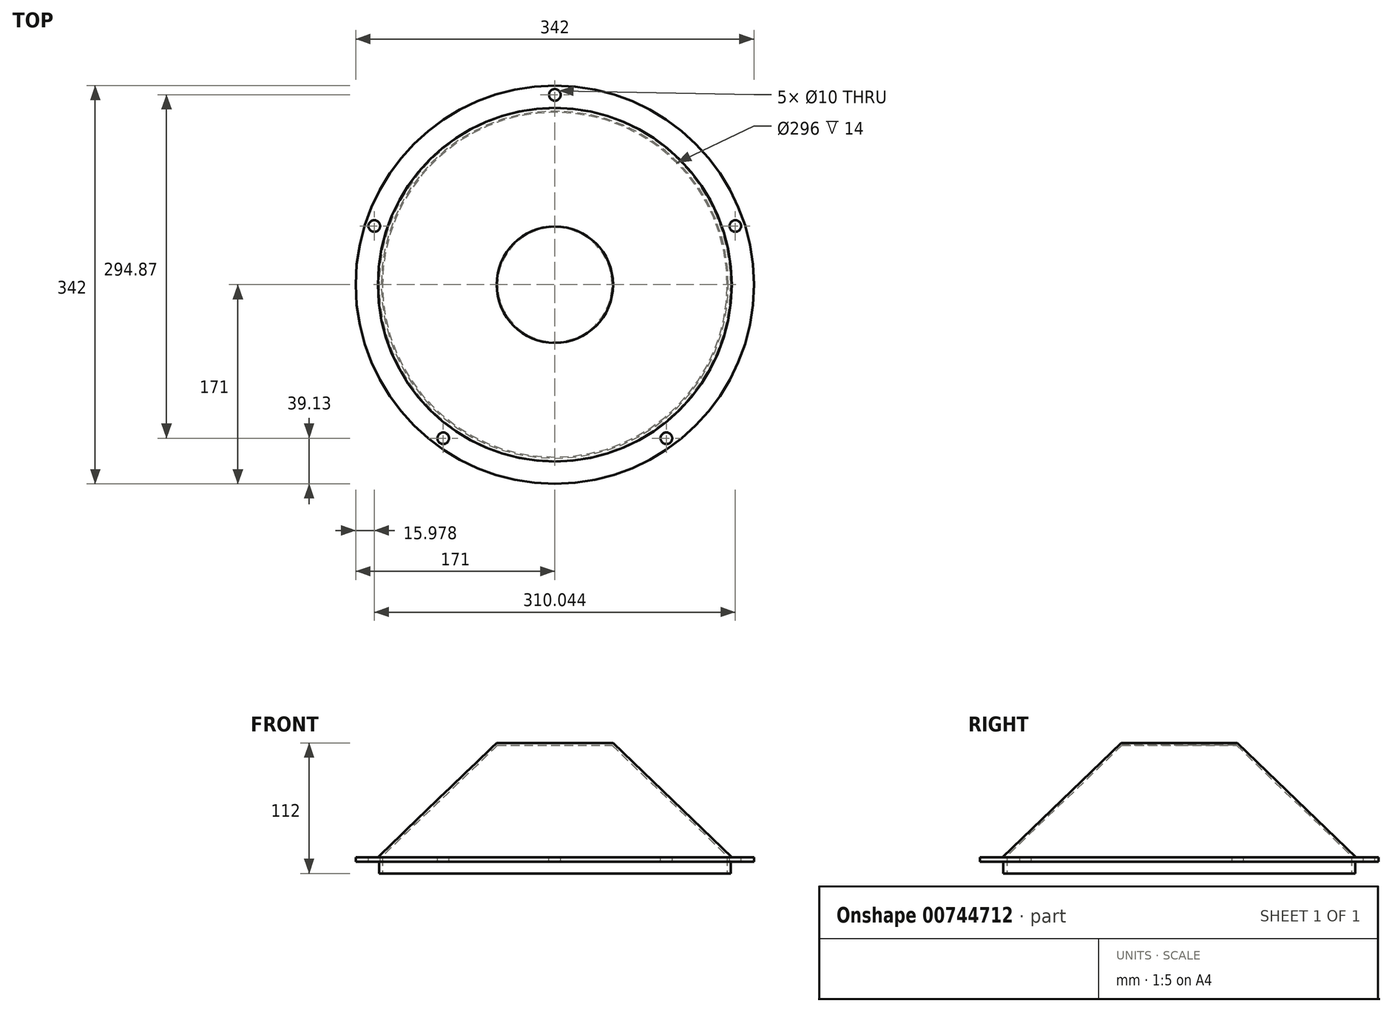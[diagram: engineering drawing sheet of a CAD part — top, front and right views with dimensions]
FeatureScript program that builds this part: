
annotation { "Feature Type Name" : "Feature", "Feature Type Description" : "" }
export const myFeature = defineFeature(function(context is Context, id is Id, definition is map)
    precondition{}
    {
        {
            var Q0;
            Q0=qCreatedBy(makeId("Top.planeOp"),FACE);
            var sketch = newSketch(context, id + "F0", { "sketchPlane" : qUnion([Q0])});
            skCircle(sketch, "E0", {"center": v(0, 0) * mm, "radius": 171 * mm});
            skCircle(sketch, "E1", {"center": v(0, 0) * mm, "radius": 148 * mm});
            skSolve(sketch);
        }
        {
            var Q0;
            Q0 = qSketchRegion(id + "F0", true);
            extrude(context, id + "F1", {"entities" : qUnion([Q0]), "depth" : 4 * mm, "offsetDistance" : 25 * mm});
        }
        {
            var Q0;
            Q0=makeQuery(id+"F1.opExtrude","CAP_FACE",FACE,{"disambiguationData":[OSD([sQuery(id+"F0.wireOp",EDGE,"E0"),sQuery(id+"F0.wireOp",EDGE,"E1")])],"isStart":false});
            var sketch = newSketch(context, id + "F2", { "sketchPlane" : qUnion([Q0])});
            skCircle(sketch, "E2", {"center": v(0, 163) * mm, "radius": 5 * mm});
            skCircle(sketch, "E3.1.0", {"center": v(-155.02, 50.37) * mm, "radius": 5 * mm});
            skCircle(sketch, "E3.2.0", {"center": v(-95.8, -131.87) * mm, "radius": 5 * mm});
            skCircle(sketch, "E3.3.0", {"center": v(95.8, -131.87) * mm, "radius": 5 * mm});
            skCircle(sketch, "E3.4.0", {"center": v(155.02, 50.37) * mm, "radius": 5 * mm});
            skPoint(sketch, "E3.center", {"position": v(0, 0) * mm});
            skSolve(sketch);
        }
        {
            var Q0;
            Q0=makeQuery(id+"F2.imprint","IMPRINT",FACE,{"disambiguationData":[TD([[makeQuery(id+"F2.imprint","IMPRINT",EDGE,{"derivedFrom":sQuery(id+"F2.wireOp",EDGE,"E2")}),1.0]])]});
            var Q1;
            Q1=makeQuery(id+"F2.imprint","IMPRINT",FACE,{"disambiguationData":[TD([[makeQuery(id+"F2.imprint","IMPRINT",EDGE,{"derivedFrom":sQuery(id+"F2.wireOp",EDGE,"E3.1.0")}),1.0]])]});
            var Q2;
            Q2=makeQuery(id+"F2.imprint","IMPRINT",FACE,{"disambiguationData":[TD([[makeQuery(id+"F2.imprint","IMPRINT",EDGE,{"derivedFrom":sQuery(id+"F2.wireOp",EDGE,"E3.4.0")}),1.0]])]});
            var Q3;
            Q3=makeQuery(id+"F2.imprint","IMPRINT",FACE,{"disambiguationData":[TD([[makeQuery(id+"F2.imprint","IMPRINT",EDGE,{"derivedFrom":sQuery(id+"F2.wireOp",EDGE,"E3.3.0")}),1.0]])]});
            var Q4;
            Q4=makeQuery(id+"F2.imprint","IMPRINT",FACE,{"disambiguationData":[TD([[makeQuery(id+"F2.imprint","IMPRINT",EDGE,{"derivedFrom":sQuery(id+"F2.wireOp",EDGE,"E3.2.0")}),1.0]])]});
            extrude(context, id + "F3", {"entities" : qUnion([Q0, Q1, Q2, Q3, Q4]), "operationType" : NewBodyOperationType.REMOVE, "endBound" : BoundingType.THROUGH_ALL, "oppositeDirection" : true, "depth" : 25 * mm, "offsetDistance" : 25 * mm});
        }
        {
            var Q0;
            Q0=makeQuery(id+"F1.opExtrude","CAP_FACE",FACE,{"disambiguationData":[OSD([sQuery(id+"F0.wireOp",EDGE,"E0"),sQuery(id+"F0.wireOp",EDGE,"E1")])],"isStart":true});
            var sketch = newSketch(context, id + "F4", { "sketchPlane" : qUnion([Q0])});
            skCircle(sketch, "E4", {"center": v(0, 0) * mm, "radius": 148 * mm});
            skCircle(sketch, "E5", {"center": v(0, 0) * mm, "radius": 151 * mm});
            skSolve(sketch);
        }
        {
            var Q0;
            Q0=makeQuery(id+"F4.imprint","IMPRINT",FACE,{"disambiguationData":[TD([[makeQuery(id+"F4.imprint","IMPRINT",EDGE,{"derivedFrom":sQuery(id+"F4.wireOp",EDGE,"E4")}),1.0]])]});
            extrude(context, id + "F5", {"entities" : qUnion([Q0]), "operationType" : NewBodyOperationType.ADD, "depth" : 10 * mm, "offsetDistance" : 25 * mm});
        }
        {
            var Q0;
            Q0=qCreatedBy(makeId("Front.planeOp"),FACE);
            cPlane(context, id + "F6", {"entities" : qUnion([Q0]), "cplaneType" : CPlaneType.OFFSET, "offset" : 0 * mm, "width" : 150 * mm, "height" : 150 * mm});
        }
        {
            var Q0;
            Q0=qCreatedBy(id+"F6.planeOp",FACE);
            var sketch = newSketch(context, id + "F7", { "sketchPlane" : qUnion([Q0])});
            skLineSegment(sketch, "E6", {"start": v(0, 0) * mm, "end": v(0, 102) * mm, "construction": true});
            skLineSegment(sketch, "E7", {"start": v(-151.89, 4) * mm, "end": v(163.57, 4) * mm, "construction": true});
            skLineSegment(sketch, "E8", {"start": v(-151.89, 4) * mm, "end": v(-50, 102) * mm});
            skLineSegment(sketch, "E9", {"start": v(-151.89, 4) * mm, "end": v(-149, 4) * mm});
            skLineSegment(sketch, "E10", {"start": v(-149, 4) * mm, "end": v(-49.2, 100) * mm});
            skLineSegment(sketch, "E11", {"start": v(0, 102) * mm, "end": v(-50, 102) * mm});
            skLineSegment(sketch, "E12", {"start": v(0, 100) * mm, "end": v(-49.2, 100) * mm});
            skLineSegment(sketch, "E13", {"start": v(0, 102) * mm, "end": v(0, 100) * mm});
            skSolve(sketch);
        }
        {
            var Q0;
            Q0=makeQuery(id+"F7.imprint","IMPRINT",FACE,{"disambiguationData":[TD([[makeQuery(id+"F7.imprint","IMPRINT",EDGE,{"derivedFrom":sQuery(id+"F7.wireOp",EDGE,"E8")}),-1.0]])]});
            var Q1;
            Q1=sQuery(id+"F7.wireOp",EDGE,"E6");
            revolve(context, id + "F8", {"operationType" : NewBodyOperationType.ADD, "surfaceOperationType" : NewSurfaceOperationType.NEW, "entities" : qUnion([Q0]), "axis" : qUnion([Q1]), "revolveType" : RevolveType.FULL});
        }
    });
